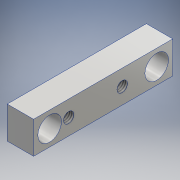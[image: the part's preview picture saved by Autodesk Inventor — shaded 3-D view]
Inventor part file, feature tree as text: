
AUTODESK INVENTOR PART (.ipt)
format: ipt  version: 2016 (Build 200138000, 138)  size: 124,928 bytes
history: native  units: mm
features: sketch x4, extrude x3, hole x1
ambient origin geometry x8: Origin, YZ Plane, XZ Plane, XY Plane, X Axis, Y Axis, Z Axis, Center Point
bodies: Solid1 (feature_tree)
feature tree (8):
  extrude  "Extrusion1"  Depth=12.3mm
  sketch  "Sketch2"  dims[d2=65.0mm d3=0.0mm d4=6.5mm]
  extrude  "Extrusion2"  Depth=65.0mm
  extrude  "Extrusion3"  Depth=11.0mm
  hole  "Hole1"  [1 undecoded]
  sketch  "Sketch4"  dims[d9=11.0mm d10=50.0mm d11=0.0mm d12=21.3mm d13=0.0mm d14=6.0mm d15=4.917mm d16=15.0mm d17=4.0mm d18=2.0mm d19=90.0deg d20=15.1mm d21=20.594885mm d22=16.395mm d23=6.0mm d24=25.0mm d26=25.0mm d27=25.0mm]
  sketch  "Sketch1"  dims[d0=15.0mm d1=12.3mm]
  sketch  "Sketch3"  dims[d5=6.5mm d8=11.0mm]
note: 1 required parameter value undecoded (feature->parameter linkage not recoverable at this tier; creation-order binding heuristic only, values carry confidence <= 0.55)
